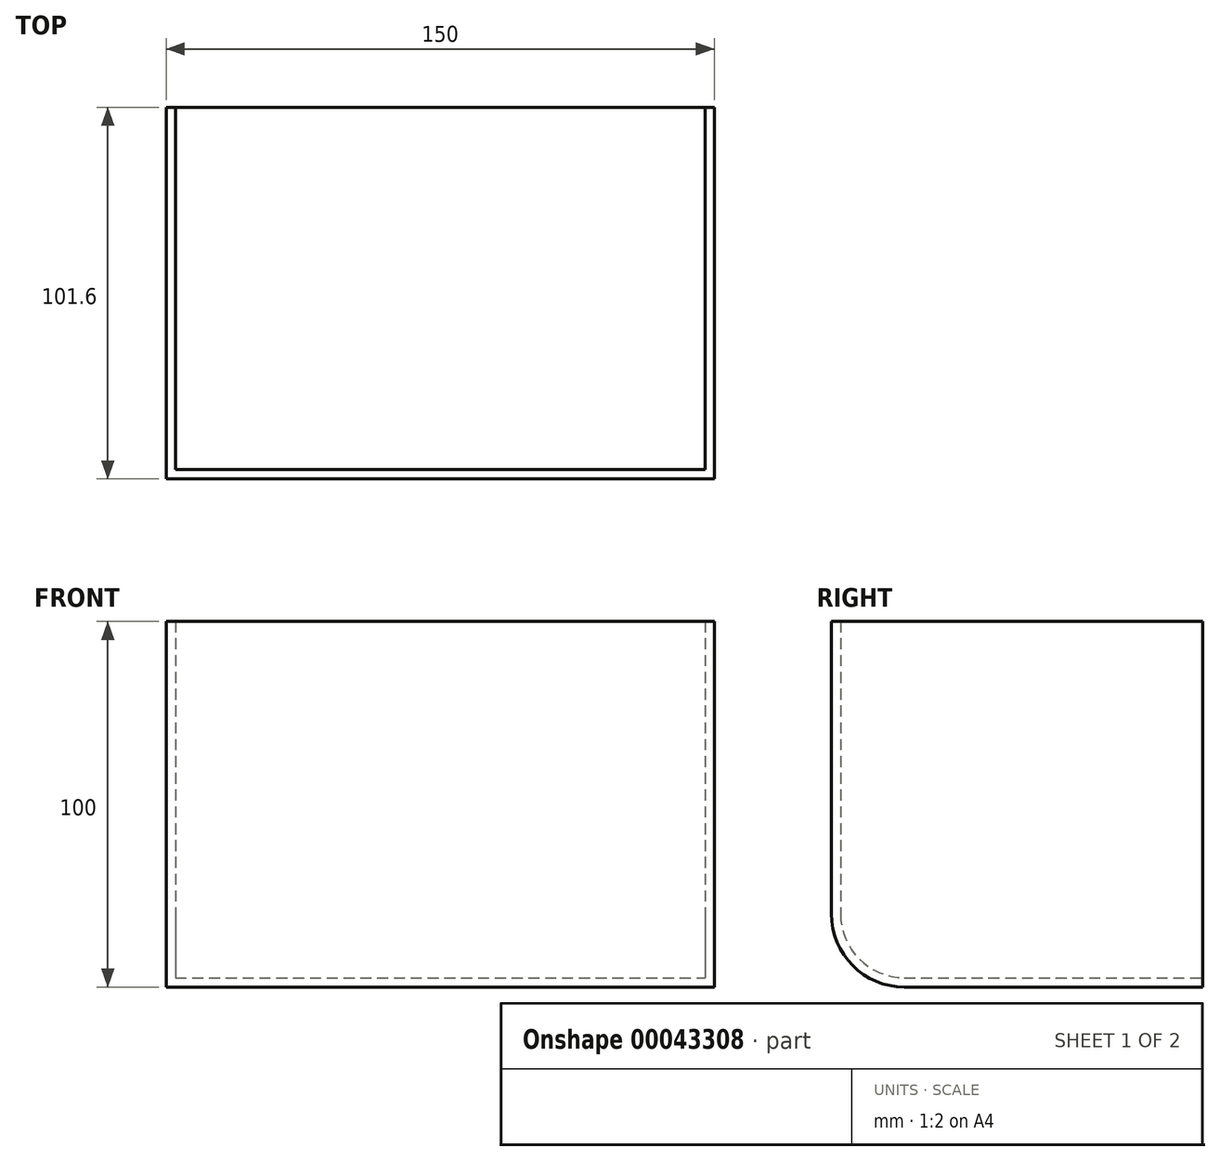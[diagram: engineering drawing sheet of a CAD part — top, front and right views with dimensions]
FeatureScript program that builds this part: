
annotation { "Feature Type Name" : "Feature", "Feature Type Description" : "" }
export const myFeature = defineFeature(function(context is Context, id is Id, definition is map)
    precondition{}
    {
        {
            var Q0;
            Q0=qCreatedBy(makeId("Front.planeOp"),FACE);
            var sketch = newSketch(context, id + "F0", { "sketchPlane" : qUnion([Q0])});
            skLineSegment(sketch, "E0.bottom", {"start": v(-110.56, 32.27) * mm, "end": v(39.44, 32.27) * mm});
            skLineSegment(sketch, "E0.top", {"start": v(-110.56, -67.73) * mm, "end": v(39.44, -67.73) * mm});
            skLineSegment(sketch, "E0.left", {"start": v(-110.56, 32.27) * mm, "end": v(-110.56, -67.73) * mm});
            skLineSegment(sketch, "E0.right", {"start": v(39.44, 32.27) * mm, "end": v(39.44, -67.73) * mm});
            skSolve(sketch);
        }
        {
            var Q0;
            Q0=makeQuery(id+"F0.imprint","IMPRINT",FACE,{"disambiguationData":[TD([[makeQuery(id+"F0.imprint","IMPRINT",EDGE,{"derivedFrom":sQuery(id+"F0.wireOp",EDGE,"E0.bottom")}),-1.0]])]});
            extrude(context, id + "F1", {"entities" : qUnion([Q0]), "depth" : 101.6 * mm});
        }
        {
            var Q0;
            Q0=makeQuery(id+"F1.opExtrude","CAP_EDGE",EDGE,{"disambiguationData":[OSD([sQuery(id+"F0.wireOp",EDGE,"E0.top")])],"isStart":false});
            fillet(context, id + "F2", {"entities" : qUnion([Q0]), "radius" : 20 * mm, "tangentPropagation" : true, "allowEdgeOverflow" : false});
        }
        {
            var Q0;
            Q0=makeQuery(id+"F1.opExtrude","CAP_FACE",FACE,{"disambiguationData":[OSD([sQuery(id+"F0.wireOp",EDGE,"E0.bottom"),sQuery(id+"F0.wireOp",EDGE,"E0.top"),sQuery(id+"F0.wireOp",EDGE,"E0.left"),sQuery(id+"F0.wireOp",EDGE,"E0.right")])],"isStart":true});
            var Q1;
            Q1=makeQuery(id+"F1.opExtrude","SWEPT_FACE",FACE,{"disambiguationData":[OSD([sQuery(id+"F0.wireOp",EDGE,"E0.bottom")])]});
            shell(context, id + "F3", {"entities" : qUnion([Q0, Q1]), "thickness" : 2.54 * mm});
        }
    });
